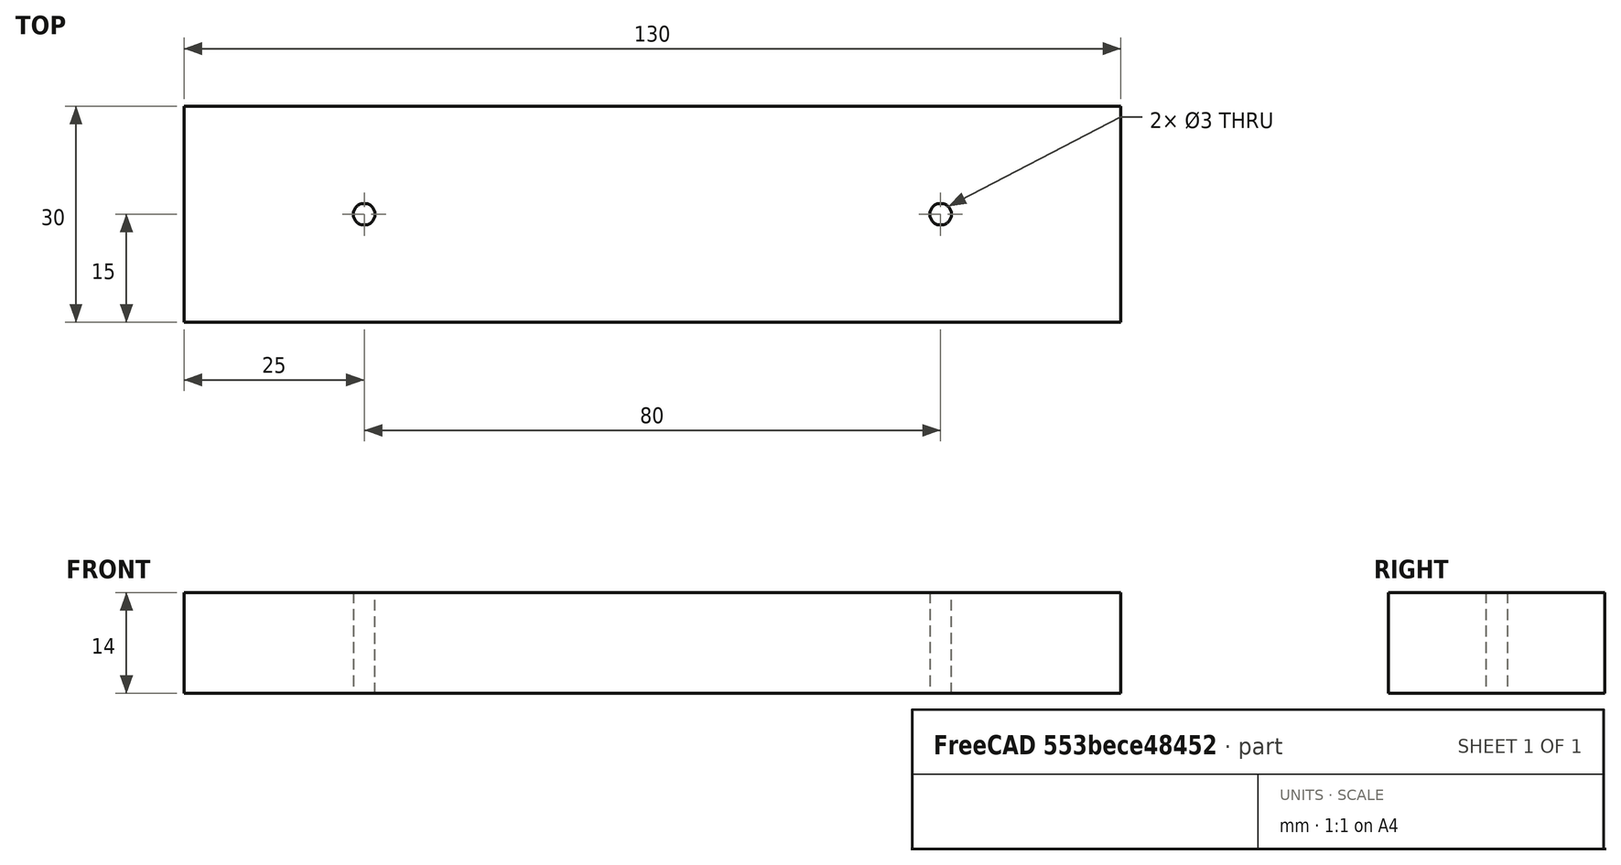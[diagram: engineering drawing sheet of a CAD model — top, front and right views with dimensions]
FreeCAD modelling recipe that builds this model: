
FCSTD DOCUMENT  (FreeCAD 0.19R24276 (Git))
Label: plate_130x30x14
License: All rights reserved
LicenseURL: http://en.wikipedia.org/wiki/All_rights_reserved
objects: Sketcher::SketchObject×1, PartDesign::Pad×1, PartDesign::Body×1
note: 4 computed .brp shape members not serialized (recipe doc carries the construction recipe); baked Part::Feature solids carry a one-line shape summary decoded from their .brp

FEATURE [Sketcher::SketchObject] Sketch
  FullyConstrained = true
  MapMode = 5
  Support = -> [XY_Plane]
  sketch-geometry (7):
    g0: LineSegment StartX=0 StartY=0 StartZ=0 EndX=130 EndY=0 EndZ=0
    g1: LineSegment StartX=130 StartY=0 StartZ=0 EndX=130 EndY=30 EndZ=0
    g2: LineSegment StartX=130 StartY=30 StartZ=0 EndX=0 EndY=30 EndZ=0
    g3: LineSegment StartX=0 StartY=30 StartZ=0 EndX=0 EndY=0 EndZ=0
    g4: Circle CenterX=25 CenterY=15 CenterZ=0 NormalX=0 NormalY=0 NormalZ=1 AngleXU=0 Radius=1.5
    g5: Circle CenterX=105 CenterY=15 CenterZ=0 NormalX=0 NormalY=0 NormalZ=1 AngleXU=0 Radius=1.5
    g6: LineSegment StartX=25 StartY=15 StartZ=0 EndX=105 EndY=15 EndZ=0
  constraints (19):
    c: Coincident(g0,g1)
    c: Coincident(g1,g2)
    c: Coincident(g2,g3)
    c: Coincident(g3,g0)
    c: Horizontal(g0)
    c: Horizontal(g2)
    c: Vertical(g1)
    c: Vertical(g3)
    c: Coincident(g0,g-1)
    c: DistanceX(g0,g0) = 130
    c: DistanceY(g3,g3) = 30
    c: Coincident(g6,g4)
    c: Coincident(g6,g5)
    c: Horizontal(g6)
    c: Diameter(g4) = 3
    c: Equal(g4,g5)
    c: DistanceX(g0,g4) = 25
    c: DistanceX(g5,g1) = 25
    c: DistanceY(g0,g4) = 15
FEATURE [PartDesign::Pad] Pad
  Direction = (1,1,1)
  Length = 14
  Length2 = 100
  Profile = -> Sketch
  Type = 0
FEATURE [PartDesign::Body] Body
  Group = -> [Sketch,Pad]
  Origin = -> Origin
  Tip = -> Pad
